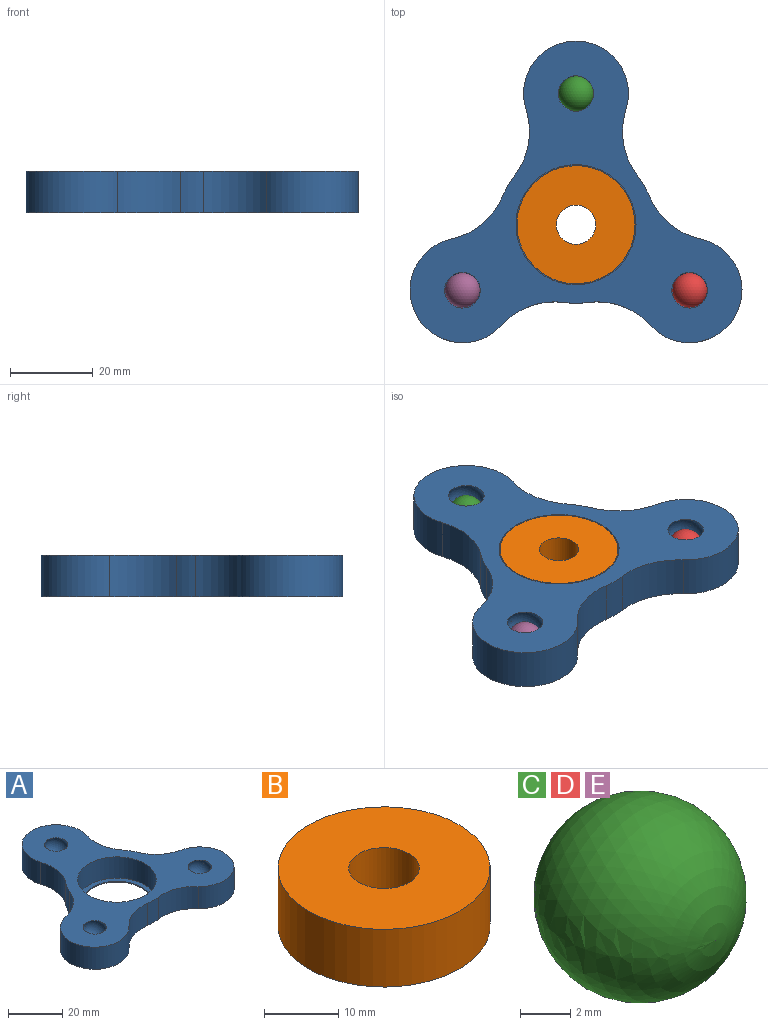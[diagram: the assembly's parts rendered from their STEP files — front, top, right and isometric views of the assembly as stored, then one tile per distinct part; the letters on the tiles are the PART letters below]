
ASSEMBLY  parts=5 mates=5
PART A: 20 faces, bbox 80.4x73x12.8 mm
  f0: cylinder r=17.38mm len=12.48mm, axis (0,0,1), area 170.6mm2, adj f1,f11,f12,f16
  f1: cylinder r=12.7mm len=25.12mm, axis (0,0,1), area 479.7mm2, adj f0,f2,f12,f16
  f2: cylinder r=17.38mm len=15.36mm, axis (0,0,1), area 170.6mm2, adj f1,f3,f12,f16
  f3: cylinder r=19.05mm len=10.03mm, axis (0,0,1), area 54.7mm2, adj f2,f4,f12,f16
  f4: cylinder r=17.38mm len=15.36mm, axis (0,0,1), area 170.6mm2, adj f3,f5,f12,f16
  f5: cylinder r=12.7mm len=25.12mm, axis (0,0,1), area 479.7mm2, adj f4,f6,f12,f16
  f6: cylinder r=17.38mm len=12.48mm, axis (0,0,1), area 170.6mm2, adj f5,f7,f12,f16
  f7: cylinder r=19.05mm len=10.03mm, axis (0,0,1), area 54.7mm2, adj f6,f8,f12,f16
  f8: cylinder r=17.38mm len=16.08mm, axis (0,0,1), area 170.6mm2, adj f7,f9,f12,f16
  f9: cylinder r=12.7mm len=25.4mm, axis (0,0,1), area 479.7mm2, adj f8,f10,f12,f16
  f10: cylinder r=17.38mm len=16.08mm, axis (0,0,1), area 170.6mm2, adj f9,f11,f12,f16
  f11: cylinder r=19.05mm len=10.03mm, axis (0,0,1), area 54.7mm2, adj f0,f10,f12,f16
  f12: plane 80.39x73.03mm, normal (0,0,-1), area 2410.5mm2, adj f0,f1,f2,f3,f4,f5,f6,f7
  f13: cylinder r=14.54mm len=29.08mm, axis (0,0,1), area 881.9mm2, adj f14,f16
  f14: plane 29.08x29.08mm, normal (0,0,1), area 167.7mm2, adj f13,f15
  f15: cylinder r=12.57mm len=25.15mm, axis (0,0,1), area 30.1mm2, adj f12,f14
  f16: plane 80.39x73.03mm, normal (0,0,1), area 2067.9mm2, adj f0,f1,f2,f3,f4,f5,f6,f7
  f17: sphere r=4.75mm, area 201.5mm2, adj f16
  f18: sphere r=4.75mm, area 201.4mm2, adj f16
  f19: sphere r=4.75mm, area 201.4mm2, adj f16
PART B: 4 faces, bbox 28.6x28.6x9.5 mm
  f0: cylinder r=4.76mm len=9.53mm, axis (0,0,-1), area 285mm2, adj f2,f3
  f1: cylinder r=14.29mm len=28.58mm, axis (0,0,-1), area 855.1mm2, adj f2,f3
  f2: plane 28.58x28.58mm, normal (0,0,1), area 570mm2, adj f0,f1
  f3: plane 28.58x28.58mm, normal (0,0,-1), area 570mm2, adj f0,f1
PART C: 1 faces, bbox 8.5x8.5x8.5 mm
  f0: sphere r=4.25mm, area 227mm2
PART D: same geometry as C
PART E: same geometry as C
PLACE A t=(-17.74,15.8,16.61)mm
PLACE B t=(-17.74,15.8,11.97)mm
PLACE C t=(-17.74,47.55,16.48)mm
PLACE D t=(9.76,-0.07,16.48)mm
PLACE E t=(-45.23,-0.07,16.48)mm
MATE ball C.f0 <-> A.f9  axis (0,0,1) through (-17.74,47.55,16.48)mm
MATE ball E.f0 <-> A.f1  axis (0,0,1) through (-45.23,-0.07,16.48)mm
MATE planar A.f3 <-> B.f0  axis (0,0,1) through (-17.74,15.8,11.85)mm
MATE ball D.f0 <-> A.f5  axis (0,0,1) through (9.76,-0.07,16.48)mm
MATE cylindrical B.f0 <-> A.f3  axis (0,0,-1) through (-17.74,15.8,16.74)mm
